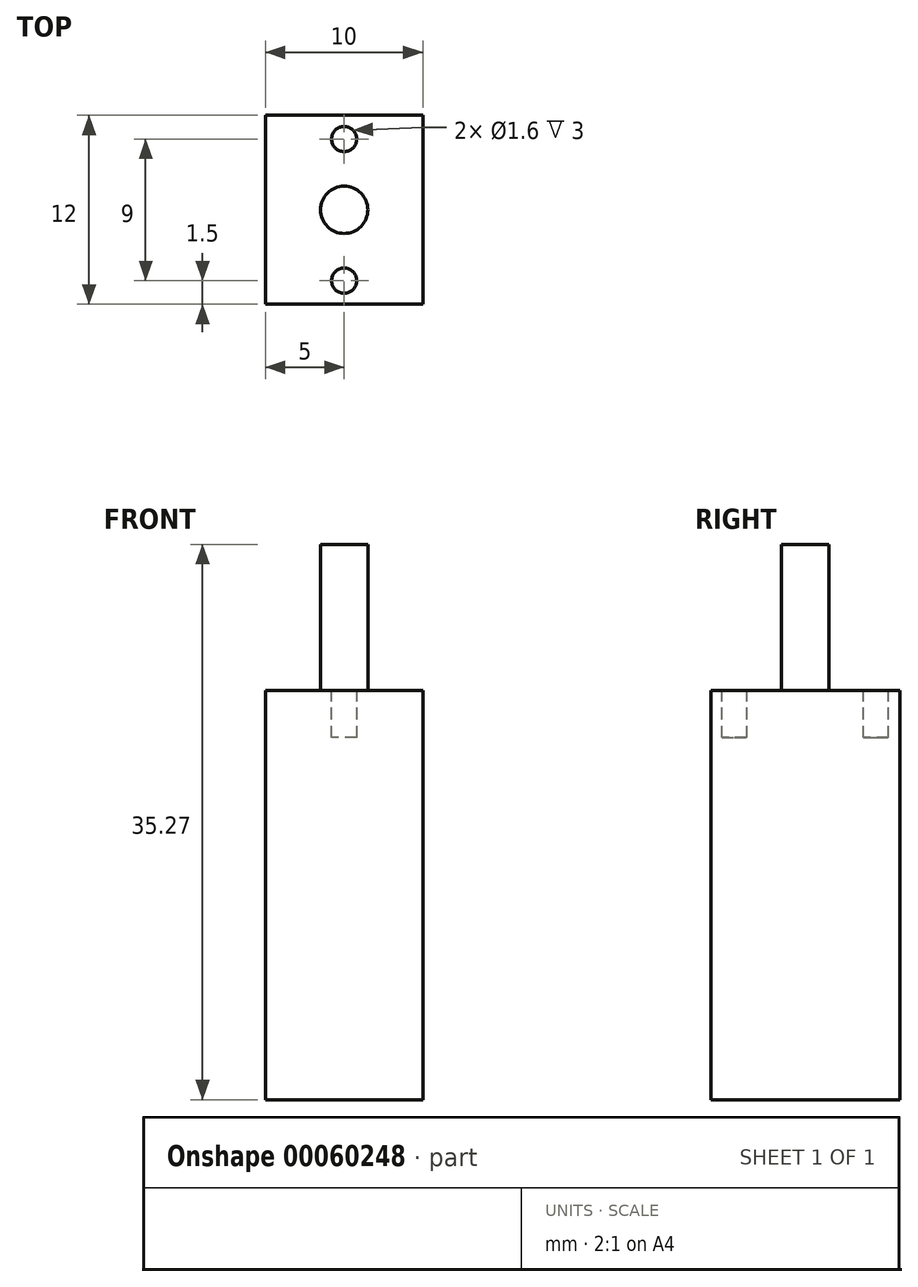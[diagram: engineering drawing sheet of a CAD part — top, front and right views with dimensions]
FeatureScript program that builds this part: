
annotation { "Feature Type Name" : "Feature", "Feature Type Description" : "" }
export const myFeature = defineFeature(function(context is Context, id is Id, definition is map)
    precondition{}
    {
        {
            var Q0;
            Q0=qCreatedBy(makeId("Top.planeOp"),FACE);
            var sketch = newSketch(context, id + "F0", { "sketchPlane" : qUnion([Q0])});
            skLineSegment(sketch, "E0.rect.bottom", {"start": v(5, -6) * mm, "end": v(-5, -6) * mm});
            skLineSegment(sketch, "E0.rect.top", {"start": v(5, 6) * mm, "end": v(-5, 6) * mm});
            skLineSegment(sketch, "E0.rect.left", {"start": v(5, -6) * mm, "end": v(5, 6) * mm});
            skLineSegment(sketch, "E0.rect.right", {"start": v(-5, -6) * mm, "end": v(-5, 6) * mm});
            skPoint(sketch, "E0.rect.middle", {"position": v(0, 0) * mm});
            skSolve(sketch);
        }
        {
            var Q0;
            Q0 = qSketchRegion(id + "F0", true);
            extrude(context, id + "F1", {"entities" : qUnion([Q0]), "depth" : 26 * mm});
        }
        {
            var Q0;
            Q0=makeQuery(id+"F1.opExtrude","CAP_FACE",FACE,{"disambiguationData":[OSD([sQuery(id+"F0.wireOp",EDGE,"E0.rect.bottom"),sQuery(id+"F0.wireOp",EDGE,"E0.rect.top"),sQuery(id+"F0.wireOp",EDGE,"E0.rect.left"),sQuery(id+"F0.wireOp",EDGE,"E0.rect.right")])],"isStart":false});
            var sketch = newSketch(context, id + "F2", { "sketchPlane" : qUnion([Q0])});
            skCircle(sketch, "E1", {"center": v(0, 0) * mm, "radius": 1.5 * mm});
            skSolve(sketch);
        }
        {
            var Q0;
            Q0 = qSketchRegion(id + "F2", true);
            extrude(context, id + "F3", {"entities" : qUnion([Q0]), "operationType" : NewBodyOperationType.ADD, "depth" : 9.27 * mm});
        }
        {
            var Q0;
            Q0=makeQuery(id+"F1.opExtrude","CAP_FACE",FACE,{"disambiguationData":[OSD([sQuery(id+"F0.wireOp",EDGE,"E0.rect.bottom"),sQuery(id+"F0.wireOp",EDGE,"E0.rect.top"),sQuery(id+"F0.wireOp",EDGE,"E0.rect.left"),sQuery(id+"F0.wireOp",EDGE,"E0.rect.right")])],"isStart":false});
            var sketch = newSketch(context, id + "F4", { "sketchPlane" : qUnion([Q0])});
            skCircle(sketch, "E2", {"center": v(0, 4.5) * mm, "radius": 0.8 * mm});
            skCircle(sketch, "E3", {"center": v(0, -4.5) * mm, "radius": 0.8 * mm});
            skLineSegment(sketch, "E4", {"start": v(0, 4.5) * mm, "end": v(0, 0) * mm, "construction": true});
            skLineSegment(sketch, "E5", {"start": v(0, 0) * mm, "end": v(0, -4.5) * mm, "construction": true});
            skSolve(sketch);
        }
        {
            var Q0;
            Q0 = qSketchRegion(id + "F4", true);
            extrude(context, id + "F5", {"entities" : qUnion([Q0]), "operationType" : NewBodyOperationType.REMOVE, "oppositeDirection" : true, "depth" : 3 * mm});
        }
    });
